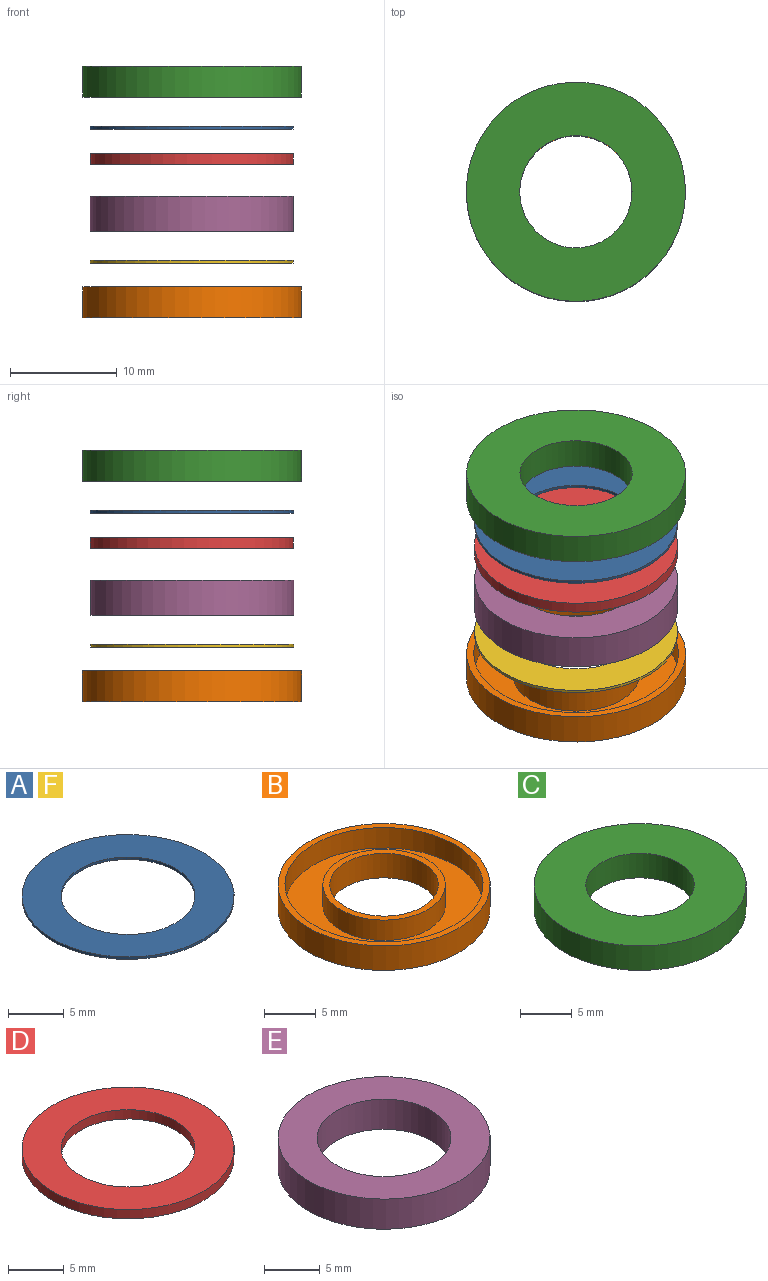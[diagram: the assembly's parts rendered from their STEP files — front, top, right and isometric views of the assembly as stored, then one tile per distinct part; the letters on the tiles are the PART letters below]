
ASSEMBLY  parts=6 mates=5
PART A: 4 faces, bbox 19x19x0.3 mm
  f0: cylinder r=6mm len=12mm, axis (0,0,-1), area 9.7mm2, adj f2,f3
  f1: cylinder r=9.5mm len=19mm, axis (0,0,-1), area 15.4mm2, adj f2,f3
  f2: plane 19x19mm, normal (0,0,1), area 170.4mm2, adj f0,f1
  f3: plane 19x19mm, normal (0,0,-1), area 170.4mm2, adj f0,f1
PART B: 8 faces, bbox 20.5x20.5x2.9 mm
  f0: plane 11.85x11.85mm, normal (0,0,1), area 23.7mm2, adj f1,f5
  f1: cylinder r=5.25mm len=10.5mm, axis (0,0,1), area 95.5mm2, adj f0,f3
  f2: cylinder r=10.25mm len=20.5mm, axis (0,0,1), area 186.5mm2, adj f3,f4
  f3: plane 20.5x20.5mm, normal (0,0,-1), area 243.5mm2, adj f1,f2
  f4: plane 20.5x20.5mm, normal (0,0,1), area 42mm2, adj f2,f6
  f5: cylinder r=5.92mm len=11.85mm, axis (0,0,-1), area 89.8mm2, adj f0,f7
  f6: cylinder r=9.57mm len=19.15mm, axis (0,0,-1), area 145.2mm2, adj f4,f7
  f7: plane 19.15x19.15mm, normal (0,0,1), area 177.7mm2, adj f5,f6
PART C: 8 faces, bbox 20.5x20.5x2.9 mm
  f0: plane 11.85x11.85mm, normal (0,0,-1), area 23.7mm2, adj f1,f5
  f1: cylinder r=5.25mm len=10.5mm, axis (0,0,-1), area 95.5mm2, adj f0,f3
  f2: cylinder r=10.25mm len=20.5mm, axis (0,0,-1), area 186.5mm2, adj f3,f4
  f3: plane 20.5x20.5mm, normal (0,0,1), area 243.5mm2, adj f1,f2
  f4: plane 20.5x20.5mm, normal (0,0,-1), area 42mm2, adj f2,f6
  f5: cylinder r=5.92mm len=11.85mm, axis (0,0,-1), area 89.8mm2, adj f0,f7
  f6: cylinder r=9.57mm len=19.15mm, axis (0,0,-1), area 145.2mm2, adj f4,f7
  f7: plane 19.15x19.15mm, normal (0,0,-1), area 177.7mm2, adj f5,f6
PART D: 4 faces, bbox 19x19x1 mm
  f0: cylinder r=6mm len=12mm, axis (0,0,-1), area 38.3mm2, adj f2,f3
  f1: cylinder r=9.5mm len=19mm, axis (0,0,-1), area 60.6mm2, adj f2,f3
  f2: plane 19x19mm, normal (0,0,1), area 170.4mm2, adj f0,f1
  f3: plane 19x19mm, normal (0,0,-1), area 170.4mm2, adj f0,f1
PART E: 4 faces, bbox 19x19x3.3 mm
  f0: cylinder r=6mm len=12mm, axis (0,0,-1), area 124.5mm2, adj f2,f3
  f1: cylinder r=9.5mm len=19mm, axis (0,0,-1), area 197.1mm2, adj f2,f3
  f2: plane 19x19mm, normal (0,0,1), area 170.4mm2, adj f0,f1
  f3: plane 19x19mm, normal (0,0,-1), area 170.4mm2, adj f0,f1
PART F: same geometry as A
PLACE A rot(axis=(0,0,1),108.9deg) t=(0,0,14.76)mm
PLACE B at identity fixed
PLACE C rot(axis=(0,0,1),77.7deg) t=(0,0,17.75)mm
PLACE D rot(axis=(0,0,1),27.5deg) t=(0,0,11.45)mm
PLACE E rot(axis=(0,0,1),44.5deg) t=(0,0,5.2)mm
PLACE F rot(axis=(0,0,1),31.1deg) t=(0,0,2.23)mm
MATE cylindrical F.f0 <-> D.f0  axis (0,0,1) through (0,0,2.48)mm
MATE cylindrical E.f0 <-> A.f0  axis (0,0,1) through (0,0,8.5)mm
MATE cylindrical D.f0 <-> E.f0  axis (0,0,1) through (0,0,12.47)mm
MATE cylindrical C.f1 <-> B.f5  axis (0,0,1) through (0,0,20.65)mm
MATE cylindrical F.f0 <-> C.f1  axis (0,0,1) through (0,0,2.48)mm
